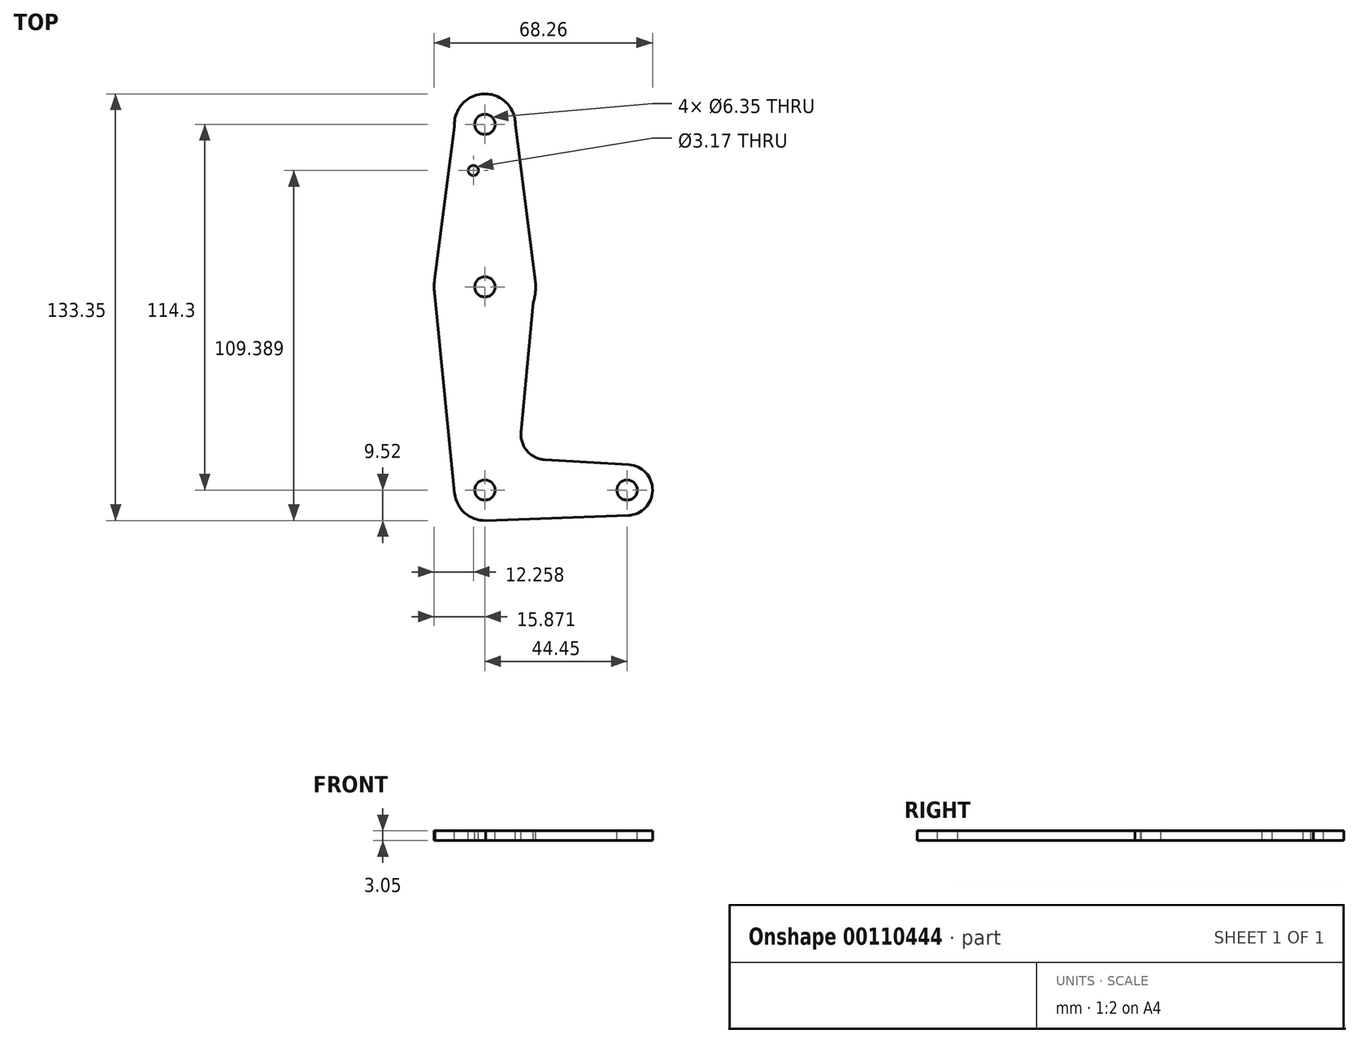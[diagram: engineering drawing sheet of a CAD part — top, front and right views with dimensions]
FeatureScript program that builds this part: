
annotation { "Feature Type Name" : "Feature", "Feature Type Description" : "" }
export const myFeature = defineFeature(function(context is Context, id is Id, definition is map)
    precondition{}
    {
        {
            var Q0;
            Q0=qCreatedBy(makeId("Top.planeOp"),FACE);
            var sketch = newSketch(context, id + "F0", { "sketchPlane" : qUnion([Q0])});
            skCircle(sketch, "E0", {"center": v(15.7, 94.03) * mm, "radius": 9.53 * mm});
            skCircle(sketch, "E1", {"center": v(15.7, 43.23) * mm, "radius": 15.88 * mm});
            skCircle(sketch, "E2", {"center": v(15.7, -20.27) * mm, "radius": 9.53 * mm});
            skCircle(sketch, "E3", {"center": v(60.15, -20.27) * mm, "radius": 7.94 * mm});
            skLineSegment(sketch, "E4", {"start": v(15.7, 94.03) * mm, "end": v(15.7, 43.23) * mm});
            skLineSegment(sketch, "E5", {"start": v(15.7, -20.27) * mm, "end": v(15.7, 43.23) * mm});
            skLineSegment(sketch, "E6", {"start": v(15.7, -20.27) * mm, "end": v(60.15, -20.27) * mm, "construction": true});
            skLineSegment(sketch, "E7", {"start": v(15.7, 94.03) * mm, "end": v(15.7, -20.27) * mm, "construction": true});
            skLineSegment(sketch, "E8", {"start": v(-0.04, 45.28) * mm, "end": v(6.21, 93.23) * mm});
            skLineSegment(sketch, "E9", {"start": v(0.1, 40.27) * mm, "end": v(6.22, -21.21) * mm});
            skLineSegment(sketch, "E10", {"start": v(25.23, 94.03) * mm, "end": v(31.45, 45.24) * mm});
            skLineSegment(sketch, "E11", {"start": v(15.93, -29.8) * mm, "end": v(60.43, -28.2) * mm});
            skPoint(sketch, "E12", {"position": v(30.98, 40.27) * mm});
            skArc(sketch, "E13.filletArc", {"start": v(26.98, -2.1) * mm, "mid": v(28.86, -8.02) * mm, "end": v(34.43, -10.79) * mm});
            skCircle(sketch, "E14", {"center": v(60.15, -20.27) * mm, "radius": 3.18 * mm});
            skCircle(sketch, "E15", {"center": v(15.7, -20.27) * mm, "radius": 3.18 * mm});
            skCircle(sketch, "E16", {"center": v(15.7, 43.23) * mm, "radius": 3.18 * mm});
            skCircle(sketch, "E17", {"center": v(15.7, 94.03) * mm, "radius": 3.18 * mm});
            skCircle(sketch, "E18", {"center": v(12.09, 79.6) * mm, "radius": 1.59 * mm});
            skLineSegment(sketch, "E19", {"start": v(34.43, -10.79) * mm, "end": v(60.62, -12.35) * mm});
            skLineSegment(sketch, "E20", {"start": v(26.98, -2.1) * mm, "end": v(31.45, 45.24) * mm});
            skSolve(sketch);
        }
        {
            var Q0;
            Q0=makeQuery(id+"F0.imprint","IMPRINT",FACE,{"disambiguationData":[TD([[makeQuery(id+"F0.imprint","IMPRINT",EDGE,{"derivedFrom":sQuery(id+"F0.wireOp",EDGE,"E14")}),-1.0]])]});
            var Q1;
            {var subQ0=sQuery(id+"F0.wireOp",EDGE,"E9");Q1=makeQuery(id+"F0.imprint","IMPRINT",FACE,{"disambiguationData":[TD([[makeQuery(id+"F0.imprint","IMPRINT",EDGE,{"derivedFrom":subQ0}),1.0]])]});}
            var Q2;
            {var subQ12=sQuery(id+"F0.wireOp",EDGE,"E13.filletArc");Q2=makeQuery(id+"F0.imprint","IMPRINT",FACE,{"disambiguationData":[TD([[makeQuery(id+"F0.imprint","IMPRINT",EDGE,{"derivedFrom":subQ12}),-1.0]])]});}
            var Q3;
            {var subQ1=sQuery(id+"F0.wireOp",EDGE,"E1");var subQ5=sQuery(id+"F0.wireOp",EDGE,"E20");var subQ6=makeQuery(id+"F0.imprint","INTERSECT",VERTEX,{"derivedFrom":[subQ1,subQ5]});Q3=makeQuery(id+"F0.imprint","IMPRINT",FACE,{"disambiguationData":[TD([[makeQuery(id+"F0.imprint","IMPRINT",EDGE,{"disambiguationData":[TD([[subQ6,1.0]])],"derivedFrom":subQ1}),1.0]])]});}
            var Q4;
            {var subQ1=sQuery(id+"F0.wireOp",EDGE,"E1");var subQ5=makeQuery(id+"F0.imprint","INTERSECT",VERTEX,{"derivedFrom":[subQ1,sQuery(id+"F0.wireOp",EDGE,"E8")]});Q4=makeQuery(id+"F0.imprint","IMPRINT",FACE,{"disambiguationData":[TD([[makeQuery(id+"F0.imprint","IMPRINT",EDGE,{"disambiguationData":[TD([[subQ5,1.0]])],"derivedFrom":subQ1}),1.0]])]});}
            var Q5;
            Q5=makeQuery(id+"F0.imprint","IMPRINT",FACE,{"disambiguationData":[TD([[makeQuery(id+"F0.imprint","IMPRINT",EDGE,{"derivedFrom":sQuery(id+"F0.wireOp",EDGE,"E15")}),-1.0]])]});
            var Q6;
            {var subQ0=sQuery(id+"F0.wireOp",EDGE,"E10");Q6=makeQuery(id+"F0.imprint","IMPRINT",FACE,{"disambiguationData":[TD([[makeQuery(id+"F0.imprint","IMPRINT",EDGE,{"derivedFrom":subQ0}),-1.0]])]});}
            var Q7;
            Q7=makeQuery(id+"F0.imprint","IMPRINT",FACE,{"disambiguationData":[TD([[makeQuery(id+"F0.imprint","IMPRINT",EDGE,{"derivedFrom":sQuery(id+"F0.wireOp",EDGE,"E17")}),-1.0]])]});
            var Q8;
            {var subQ0=sQuery(id+"F0.wireOp",EDGE,"E11");var subQ1=sQuery(id+"F0.wireOp",EDGE,"E2");var subQ2=makeQuery(id+"F0.imprint","INTERSECT",VERTEX,{"disambiguationData":[OD(0.0)],"derivedFrom":[subQ1,subQ0]});Q8=makeQuery(id+"F0.imprint","IMPRINT",FACE,{"disambiguationData":[TD([[makeQuery(id+"F0.imprint","IMPRINT",EDGE,{"disambiguationData":[TD([[subQ2,-1.0]])],"derivedFrom":subQ1}),1.0]])]});}
            var Q9;
            {var subQ0=sQuery(id+"F0.wireOp",EDGE,"E20");var subQ1=sQuery(id+"F0.wireOp",EDGE,"E1");var subQ3=makeQuery(id+"F0.imprint","INTERSECT",VERTEX,{"derivedFrom":[subQ1,subQ0]});Q9=makeQuery(id+"F0.imprint","IMPRINT",FACE,{"disambiguationData":[TD([[makeQuery(id+"F0.imprint","IMPRINT",EDGE,{"disambiguationData":[TD([[subQ3,-1.0]])],"derivedFrom":subQ1}),1.0]])]});}
            var Q10;
            {var subQ5=sQuery(id+"F0.wireOp",EDGE,"E8");Q10=makeQuery(id+"F0.imprint","IMPRINT",FACE,{"disambiguationData":[TD([[makeQuery(id+"F0.imprint","IMPRINT",EDGE,{"derivedFrom":subQ5}),-1.0]])]});}
            extrude(context, id + "F1", {"entities" : qUnion([Q0, Q1, Q2, Q3, Q4, Q5, Q6, Q7, Q8, Q9, Q10]), "oppositeDirection" : true, "depth" : 3.05 * mm});
        }
    });
